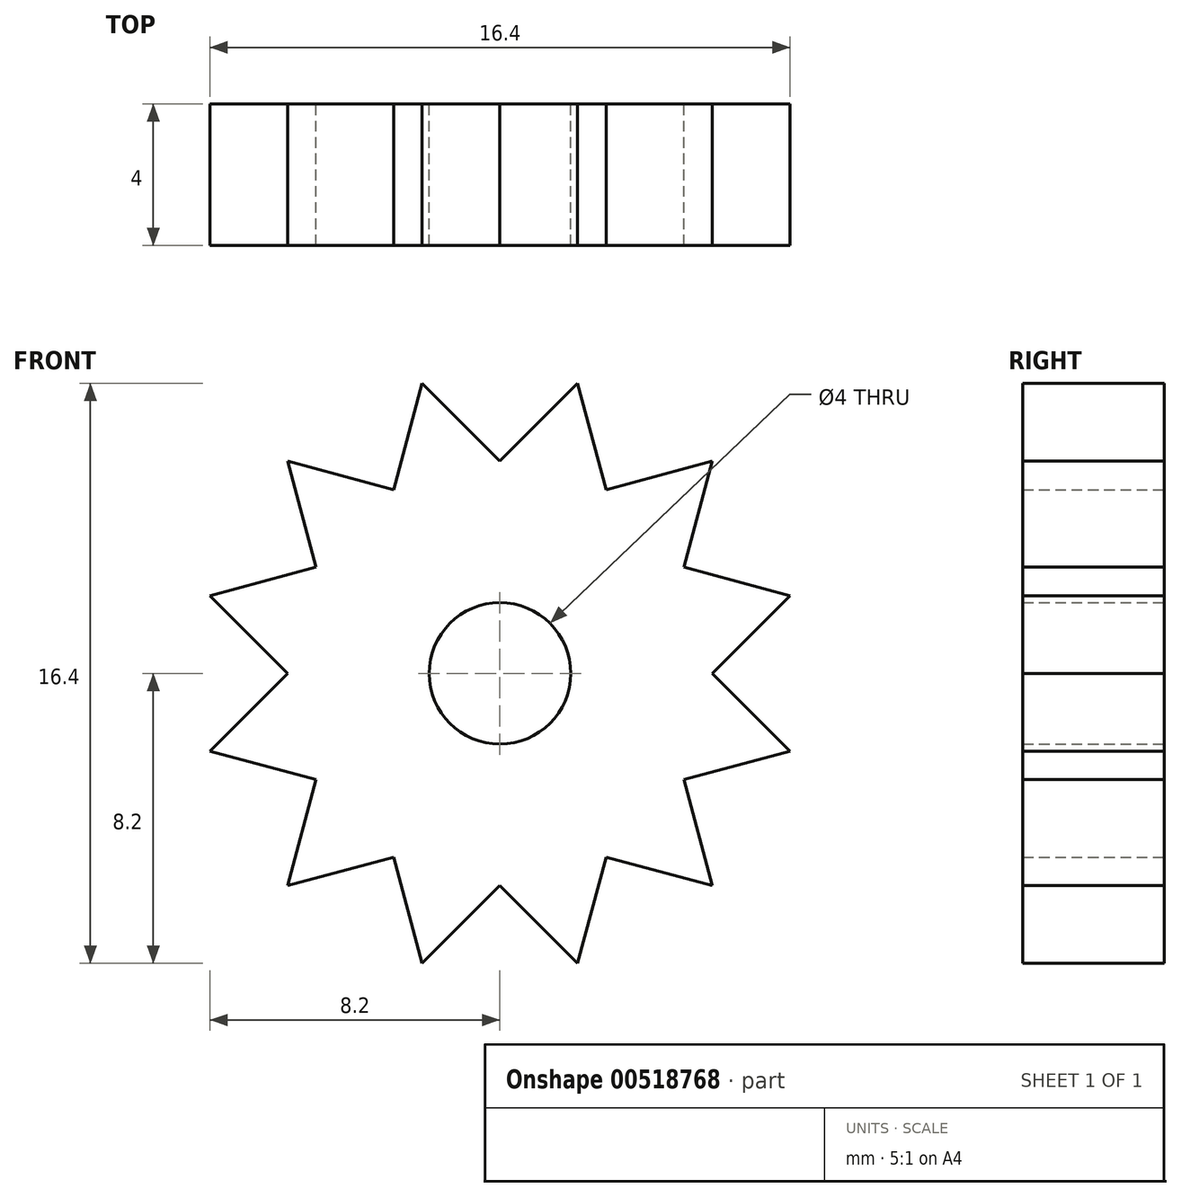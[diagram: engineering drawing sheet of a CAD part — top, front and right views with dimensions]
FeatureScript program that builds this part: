
annotation { "Feature Type Name" : "Feature", "Feature Type Description" : "" }
export const myFeature = defineFeature(function(context is Context, id is Id, definition is map)
    precondition{}
    {
        {
            var Q0;
            Q0=qCreatedBy(makeId("Front.planeOp"),FACE);
            var sketch = newSketch(context, id + "F0", { "sketchPlane" : qUnion([Q0])});
            skCircle(sketch, "E0", {"center": v(0, 0) * mm, "radius": 6 * mm});
            skCircle(sketch, "E1", {"center": v(0, 0) * mm, "radius": 2 * mm});
            skLineSegment(sketch, "E2", {"start": v(0, 0) * mm, "end": v(-3, 5.2) * mm, "construction": true});
            skLineSegment(sketch, "E3", {"start": v(-3, 5.2) * mm, "end": v(-2.2, 8.2) * mm});
            skLineSegment(sketch, "E4", {"start": v(-2.2, 8.2) * mm, "end": v(0, 6) * mm});
            skLineSegment(sketch, "E5.1.0", {"start": v(-5.2, 3) * mm, "end": v(-6, 6) * mm});
            skLineSegment(sketch, "E5.1.1", {"start": v(-6, 6) * mm, "end": v(-3, 5.2) * mm});
            skLineSegment(sketch, "E5.2.0", {"start": v(-6, 0) * mm, "end": v(-8.2, 2.2) * mm});
            skLineSegment(sketch, "E5.2.1", {"start": v(-8.2, 2.2) * mm, "end": v(-5.2, 3) * mm});
            skLineSegment(sketch, "E5.3.0", {"start": v(-5.2, -3) * mm, "end": v(-8.2, -2.2) * mm});
            skLineSegment(sketch, "E5.3.1", {"start": v(-8.2, -2.2) * mm, "end": v(-6, 0) * mm});
            skLineSegment(sketch, "E5.4.0", {"start": v(-3, -5.2) * mm, "end": v(-6, -6) * mm});
            skLineSegment(sketch, "E5.4.1", {"start": v(-6, -6) * mm, "end": v(-5.2, -3) * mm});
            skLineSegment(sketch, "E5.5.0", {"start": v(0, -6) * mm, "end": v(-2.2, -8.2) * mm});
            skLineSegment(sketch, "E5.5.1", {"start": v(-2.2, -8.2) * mm, "end": v(-3, -5.2) * mm});
            skLineSegment(sketch, "E5.6.0", {"start": v(3, -5.2) * mm, "end": v(2.2, -8.2) * mm});
            skLineSegment(sketch, "E5.6.1", {"start": v(2.2, -8.2) * mm, "end": v(0, -6) * mm});
            skLineSegment(sketch, "E5.7.0", {"start": v(5.2, -3) * mm, "end": v(6, -6) * mm});
            skLineSegment(sketch, "E5.7.1", {"start": v(6, -6) * mm, "end": v(3, -5.2) * mm});
            skLineSegment(sketch, "E5.8.0", {"start": v(6, 0) * mm, "end": v(8.2, -2.2) * mm});
            skLineSegment(sketch, "E5.8.1", {"start": v(8.2, -2.2) * mm, "end": v(5.2, -3) * mm});
            skLineSegment(sketch, "E5.9.0", {"start": v(5.2, 3) * mm, "end": v(8.2, 2.2) * mm});
            skLineSegment(sketch, "E5.9.1", {"start": v(8.2, 2.2) * mm, "end": v(6, 0) * mm});
            skLineSegment(sketch, "E5.10.0", {"start": v(3, 5.2) * mm, "end": v(6, 6) * mm});
            skLineSegment(sketch, "E5.10.1", {"start": v(6, 6) * mm, "end": v(5.2, 3) * mm});
            skLineSegment(sketch, "E5.11.0", {"start": v(0, 6) * mm, "end": v(2.2, 8.2) * mm});
            skLineSegment(sketch, "E5.11.1", {"start": v(2.2, 8.2) * mm, "end": v(3, 5.2) * mm});
            skSolve(sketch);
        }
        {
            var Q0;
            Q0=qSketchRegion(id+"F0",true);
            extrude(context, id + "F1", {"entities" : qUnion([Q0]), "endBound" : BoundingType.SYMMETRIC, "depth" : 4 * mm, "offsetDistance" : 25 * mm});
        }
    });
